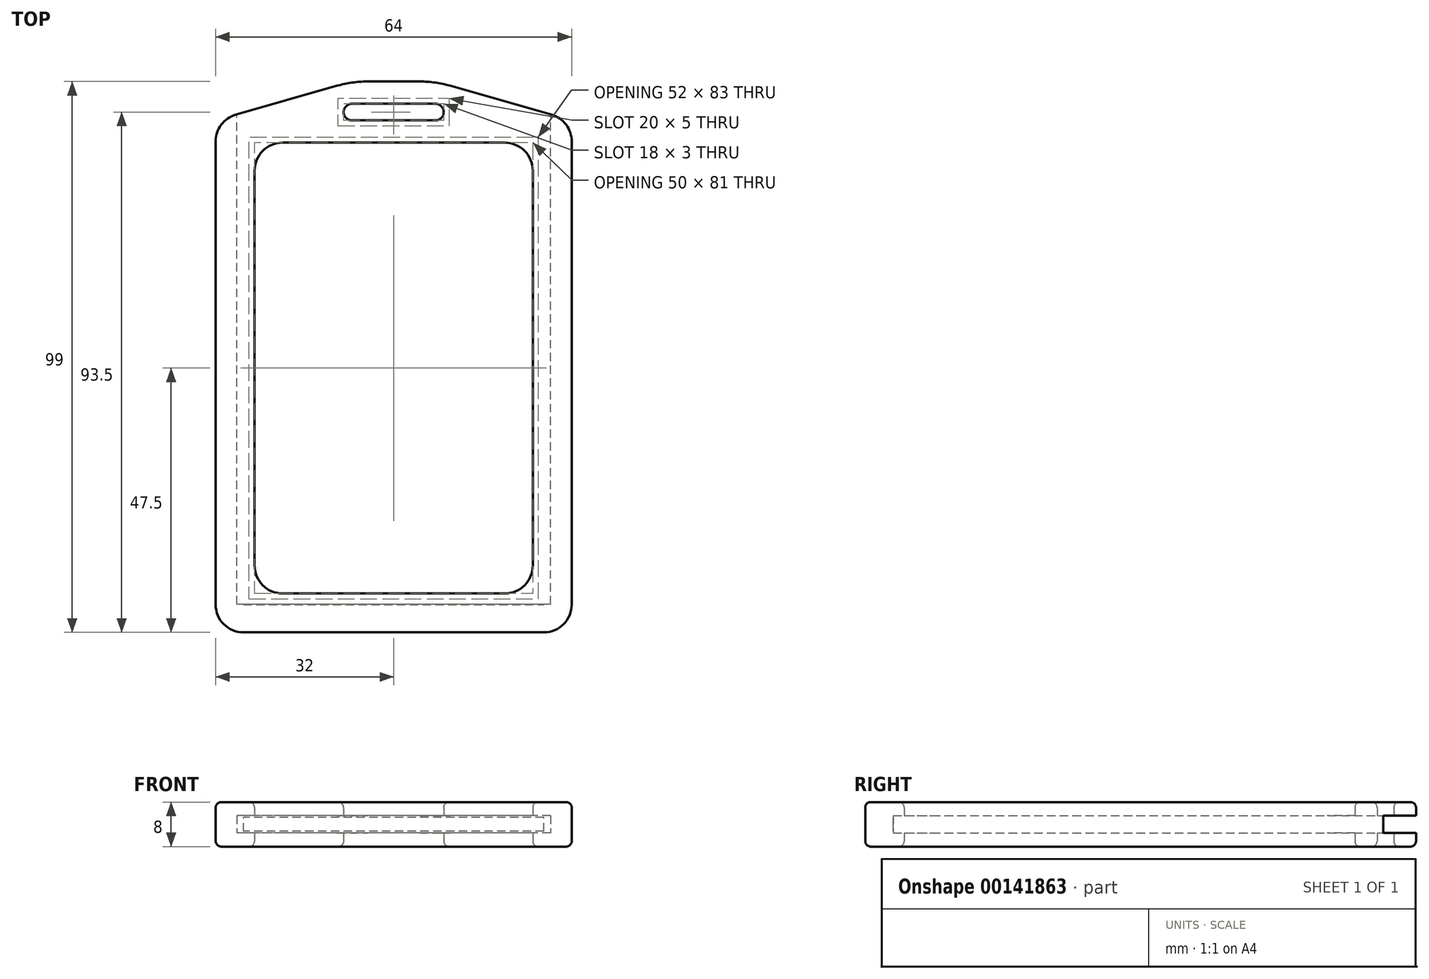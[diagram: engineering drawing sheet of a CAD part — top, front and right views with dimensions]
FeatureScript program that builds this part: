
annotation { "Feature Type Name" : "Feature", "Feature Type Description" : "" }
export const myFeature = defineFeature(function(context is Context, id is Id, definition is map)
    precondition{}
    {
        {
            var Q0;
            Q0=qCreatedBy(makeId("Top.planeOp"),FACE);
            var sketch = newSketch(context, id + "F0", { "sketchPlane" : qUnion([Q0])});
            skLineSegment(sketch, "E0.rect.bottom", {"start": v(-27, 42.5) * mm, "end": v(27, 42.5) * mm});
            skLineSegment(sketch, "E0.rect.top", {"start": v(-27, -42.5) * mm, "end": v(27, -42.5) * mm});
            skLineSegment(sketch, "E0.rect.left", {"start": v(-27, 42.5) * mm, "end": v(-27, -42.5) * mm});
            skLineSegment(sketch, "E0.rect.right", {"start": v(27, 42.5) * mm, "end": v(27, -42.5) * mm});
            skPoint(sketch, "E0.rect.middle", {"position": v(0, 0) * mm});
            skSolve(sketch);
        }
        {
            var Q0;
            Q0=makeQuery(id+"F0.imprint","IMPRINT",FACE,{"disambiguationData":[TD([[makeQuery(id+"F0.imprint","IMPRINT",EDGE,{"derivedFrom":sQuery(id+"F0.wireOp",EDGE,"E0.rect.bottom")}),-1.0]])]});
            extrude(context, id + "F1", {"entities" : qUnion([Q0]), "depth" : 2.5 * mm});
        }
        {
            var Q0;
            Q0=qCreatedBy(makeId("Top.planeOp"),FACE);
            var sketch = newSketch(context, id + "F2", { "sketchPlane" : qUnion([Q0])});
            skLineSegment(sketch, "E1", {"start": v(-32, -47.5) * mm, "end": v(-32, 44.5) * mm});
            skLineSegment(sketch, "E2", {"start": v(32, 44.5) * mm, "end": v(32, -47.5) * mm});
            skLineSegment(sketch, "E3", {"start": v(32, -47.5) * mm, "end": v(-32, -47.5) * mm});
            skLineSegment(sketch, "E4", {"start": v(-7.5, 47.5) * mm, "end": v(7.5, 47.5) * mm});
            skLineSegment(sketch, "E5", {"start": v(-7.5, 44.5) * mm, "end": v(7.5, 44.5) * mm});
            skArc(sketch, "E6", {"start": v(-7.5, 47.5) * mm, "mid": v(-9, 46) * mm, "end": v(-7.5, 44.5) * mm});
            skArc(sketch, "E7", {"start": v(7.5, 47.5) * mm, "mid": v(9, 46) * mm, "end": v(7.5, 44.5) * mm});
            skLineSegment(sketch, "E8.rect.bottom", {"start": v(-25, 40.5) * mm, "end": v(25, 40.5) * mm});
            skLineSegment(sketch, "E8.rect.top", {"start": v(-25, -40.5) * mm, "end": v(25, -40.5) * mm});
            skLineSegment(sketch, "E8.rect.left", {"start": v(-25, 40.5) * mm, "end": v(-25, -40.5) * mm});
            skLineSegment(sketch, "E8.rect.right", {"start": v(25, 40.5) * mm, "end": v(25, -40.5) * mm});
            skPoint(sketch, "E8.rect.middle", {"position": v(0, 0) * mm});
            skLineSegment(sketch, "E9", {"start": v(-32, 44.5) * mm, "end": v(-7.5, 51.5) * mm});
            skLineSegment(sketch, "E10", {"start": v(-7.5, 51.5) * mm, "end": v(7.5, 51.5) * mm});
            skLineSegment(sketch, "E11", {"start": v(7.5, 51.5) * mm, "end": v(32, 44.5) * mm});
            skSolve(sketch);
        }
        {
            var Q0;
            Q0=makeQuery(id+"F2.imprint","IMPRINT",FACE,{"disambiguationData":[TD([[makeQuery(id+"F2.imprint","IMPRINT",EDGE,{"derivedFrom":sQuery(id+"F2.wireOp",EDGE,"E1")}),-1.0]])]});
            extrude(context, id + "F3", {"entities" : qUnion([Q0]), "depth" : 8 * mm});
        }
        {
            var Q0;
            Q0=makeQuery(id+"F3.opExtrude","SWEPT_EDGE",EDGE,{"disambiguationData":[OSD([sQuery(id+"F2.wireOp",EDGE,"E1"),sQuery(id+"F2.wireOp",EDGE,"bdb59242-d5a5-46b9-b7b7-c48a45b36775")])]});
            var Q1;
            Q1=makeQuery(id+"F3.opExtrude","SWEPT_EDGE",EDGE,{"disambiguationData":[OSD([sQuery(id+"F2.wireOp",EDGE,"daee0165-ca23-428e-b79d-c411e0a02959"),sQuery(id+"F2.wireOp",EDGE,"E2")])]});
            var Q2;
            Q2=makeQuery(id+"F3.opExtrude","SWEPT_EDGE",EDGE,{"disambiguationData":[OSD([sQuery(id+"F2.wireOp",EDGE,"E2"),sQuery(id+"F2.wireOp",EDGE,"E3")])]});
            var Q3;
            Q3=makeQuery(id+"F3.opExtrude","SWEPT_EDGE",EDGE,{"disambiguationData":[OSD([sQuery(id+"F2.wireOp",EDGE,"E1"),sQuery(id+"F2.wireOp",EDGE,"E3")])]});
            fillet(context, id + "F4", {"entities" : qUnion([Q0, Q1, Q2, Q3]), "radius" : 5 * mm, "tangentPropagation" : true, "allowEdgeOverflow" : false});
        }
        {
            var Q0;
            Q0=makeQuery(id+"F3.opExtrude","SWEPT_EDGE",EDGE,{"disambiguationData":[OSD([sQuery(id+"F2.wireOp",EDGE,"E9"),sQuery(id+"F2.wireOp",EDGE,"E10")])]});
            var Q1;
            Q1=makeQuery(id+"F3.opExtrude","SWEPT_EDGE",EDGE,{"disambiguationData":[OSD([sQuery(id+"F2.wireOp",EDGE,"E10"),sQuery(id+"F2.wireOp",EDGE,"E11")])]});
            fillet(context, id + "F5", {"entities" : qUnion([Q0, Q1]), "radius" : 20 * mm, "tangentPropagation" : true, "allowEdgeOverflow" : false});
        }
        {
            var Q0;
            Q0=makeQuery(id+"F3.opExtrude","CAP_EDGE",EDGE,{"disambiguationData":[OSD([sQuery(id+"F2.wireOp",EDGE,"E4")])],"isStart":false});
            var Q1;
            Q1=makeQuery(id+"F3.opExtrude","CAP_EDGE",EDGE,{"disambiguationData":[OSD([sQuery(id+"F2.wireOp",EDGE,"E4")])],"isStart":true});
            fillet(context, id + "F6", {"entities" : qUnion([Q0, Q1]), "radius" : 1 * mm, "tangentPropagation" : true, "allowEdgeOverflow" : false});
        }
        {
            var Q0;
            Q0=makeQuery(id+"F3.opExtrude","SWEPT_EDGE",EDGE,{"disambiguationData":[OSD([sQuery(id+"F2.wireOp",EDGE,"E8.rect.bottom"),sQuery(id+"F2.wireOp",EDGE,"E8.rect.left")])]});
            var Q1;
            Q1=makeQuery(id+"F3.opExtrude","SWEPT_EDGE",EDGE,{"disambiguationData":[OSD([sQuery(id+"F2.wireOp",EDGE,"E8.rect.bottom"),sQuery(id+"F2.wireOp",EDGE,"E8.rect.right")])]});
            var Q2;
            Q2=makeQuery(id+"F3.opExtrude","SWEPT_EDGE",EDGE,{"disambiguationData":[OSD([sQuery(id+"F2.wireOp",EDGE,"E8.rect.top"),sQuery(id+"F2.wireOp",EDGE,"E8.rect.right")])]});
            var Q3;
            Q3=makeQuery(id+"F3.opExtrude","SWEPT_EDGE",EDGE,{"disambiguationData":[OSD([sQuery(id+"F2.wireOp",EDGE,"E8.rect.top"),sQuery(id+"F2.wireOp",EDGE,"E8.rect.left")])]});
            fillet(context, id + "F7", {"entities" : qUnion([Q0, Q1, Q2, Q3]), "radius" : 5 * mm, "tangentPropagation" : true, "allowEdgeOverflow" : false});
        }
        {
            var Q0;
            Q0=makeQuery(id+"F3.opExtrude","CAP_EDGE",EDGE,{"disambiguationData":[OSD([sQuery(id+"F2.wireOp",EDGE,"E8.rect.bottom")])],"isStart":false});
            var Q1;
            Q1=makeQuery(id+"F3.opExtrude","CAP_EDGE",EDGE,{"disambiguationData":[OSD([sQuery(id+"F2.wireOp",EDGE,"E8.rect.bottom")])],"isStart":true});
            var Q2;
            {var subQ0=sQuery(id+"F2.wireOp",EDGE,"E1");var subQ1=sQuery(id+"F2.wireOp",EDGE,"E3");Q2=makeQuery(id+"F4.opFillet","BLEND_EDGE",EDGE,{"blendedFrom":[makeQuery(id+"F3.opExtrude","SWEPT_EDGE",EDGE,{"disambiguationData":[OSD([subQ0,subQ1])]}),makeQuery(id+"F3.opExtrude","CAP_FACE",FACE,{"disambiguationData":[OSD([subQ0,sQuery(id+"F2.wireOp",EDGE,"bdb59242-d5a5-46b9-b7b7-c48a45b36775"),sQuery(id+"F2.wireOp",EDGE,"823fc3bd-2c2f-4f9b-bb1d-b0eb3bebb9c6"),sQuery(id+"F2.wireOp",EDGE,"daee0165-ca23-428e-b79d-c411e0a02959"),sQuery(id+"F2.wireOp",EDGE,"E2"),subQ1,sQuery(id+"F2.wireOp",EDGE,"E4"),sQuery(id+"F2.wireOp",EDGE,"E5"),sQuery(id+"F2.wireOp",EDGE,"E6"),sQuery(id+"F2.wireOp",EDGE,"E7"),sQuery(id+"F2.wireOp",EDGE,"E8.rect.bottom"),sQuery(id+"F2.wireOp",EDGE,"E8.rect.top"),sQuery(id+"F2.wireOp",EDGE,"E8.rect.left"),sQuery(id+"F2.wireOp",EDGE,"E8.rect.right")])],"isStart":false})],"blendedInto":[makeQuery(id+"F3.opExtrude","CAP_FACE",FACE,{"disambiguationData":[OSD([subQ0,sQuery(id+"F2.wireOp",EDGE,"bdb59242-d5a5-46b9-b7b7-c48a45b36775"),sQuery(id+"F2.wireOp",EDGE,"823fc3bd-2c2f-4f9b-bb1d-b0eb3bebb9c6"),sQuery(id+"F2.wireOp",EDGE,"daee0165-ca23-428e-b79d-c411e0a02959"),sQuery(id+"F2.wireOp",EDGE,"E2"),subQ1,sQuery(id+"F2.wireOp",EDGE,"E4"),sQuery(id+"F2.wireOp",EDGE,"E5"),sQuery(id+"F2.wireOp",EDGE,"E6"),sQuery(id+"F2.wireOp",EDGE,"E7"),sQuery(id+"F2.wireOp",EDGE,"E8.rect.bottom"),sQuery(id+"F2.wireOp",EDGE,"E8.rect.top"),sQuery(id+"F2.wireOp",EDGE,"E8.rect.left"),sQuery(id+"F2.wireOp",EDGE,"E8.rect.right")])],"isStart":false})]});}
            var Q3;
            Q3=makeQuery(id+"F3.opExtrude","CAP_EDGE",EDGE,{"disambiguationData":[OSD([sQuery(id+"F2.wireOp",EDGE,"E3")])],"isStart":true});
            fillet(context, id + "F8", {"entities" : qUnion([Q0, Q1, Q2, Q3]), "radius" : 1 * mm, "tangentPropagation" : true, "allowEdgeOverflow" : false});
        }
        {
            var Q0;
            Q0=makeQuery(id+"F1.opExtrude","SWEPT_BODY",BODY,{"disambiguationData":[OSD([sQuery(id+"F0.wireOp",EDGE,"E0.rect.bottom"),sQuery(id+"F0.wireOp",EDGE,"E0.rect.top"),sQuery(id+"F0.wireOp",EDGE,"E0.rect.left"),sQuery(id+"F0.wireOp",EDGE,"E0.rect.right")])]});
            transform(context, id + "F9", {"entities" : qUnion([Q0]), "transformType" : TransformType.TRANSLATION_3D, "dx" : 0 * mm, "dy" : 0 * mm, "dz" : 2.75 * mm, "makeCopy" : false});
        }
        {
            var Q0;
            Q0=makeQuery(id+"F3.opExtrude","SWEPT_FACE",FACE,{"disambiguationData":[OSD([sQuery(id+"F2.wireOp",EDGE,"E10")])]});
            var sketch = newSketch(context, id + "F10", { "sketchPlane" : qUnion([Q0])});
            skLineSegment(sketch, "E12.bottom", {"start": v(-28.2, 5.55) * mm, "end": v(28.2, 5.55) * mm});
            skLineSegment(sketch, "E12.top", {"start": v(-28.2, 2.45) * mm, "end": v(28.2, 2.45) * mm});
            skLineSegment(sketch, "E12.left", {"start": v(-28.2, 5.55) * mm, "end": v(-28.2, 2.45) * mm});
            skLineSegment(sketch, "E12.right", {"start": v(28.2, 5.55) * mm, "end": v(28.2, 2.45) * mm});
            skSolve(sketch);
        }
        {
            var Q0;
            Q0=qSketchRegion(id+"F10",true);
            extrude(context, id + "F11", {"entities" : qUnion([Q0]), "operationType" : NewBodyOperationType.REMOVE, "oppositeDirection" : true, "depth" : 93.95 * mm});
        }
    });
